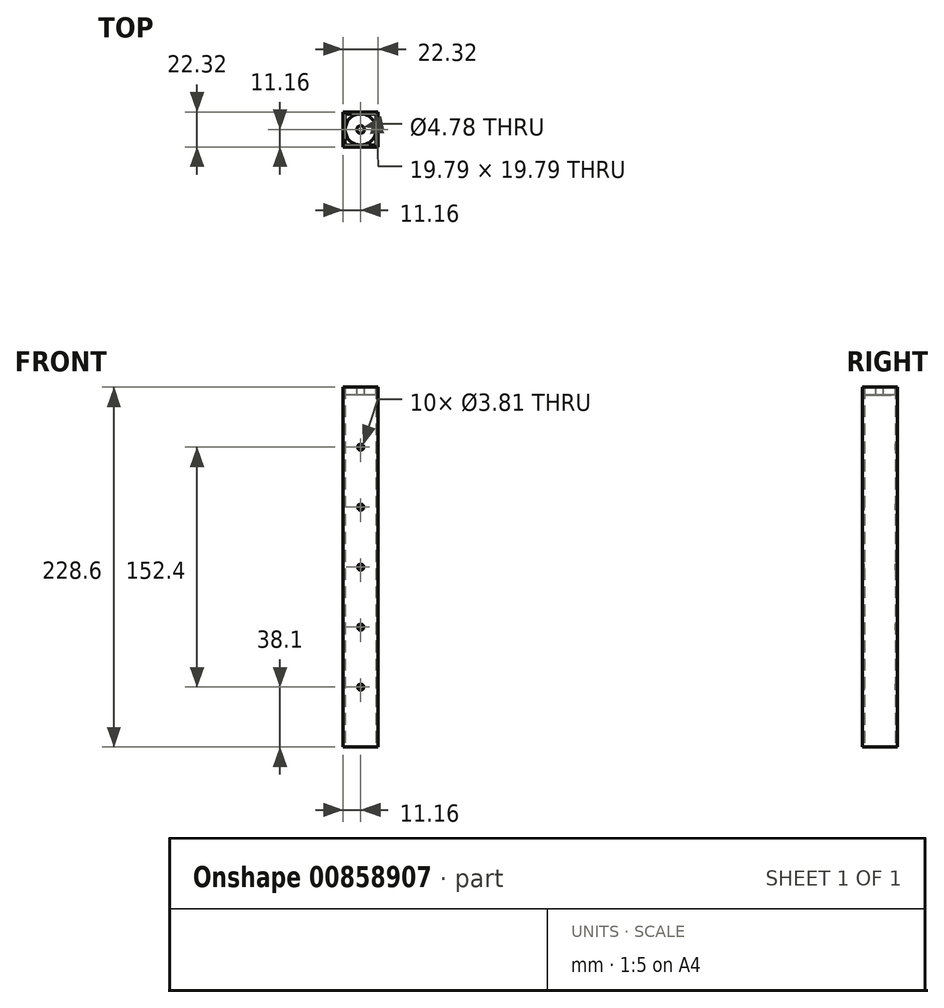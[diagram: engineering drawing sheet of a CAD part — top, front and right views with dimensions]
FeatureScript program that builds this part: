
annotation { "Feature Type Name" : "Feature", "Feature Type Description" : "" }
export const myFeature = defineFeature(function(context is Context, id is Id, definition is map)
    precondition{}
    {
        {
            var Q0;
            Q0=qCreatedBy(makeId("Top.planeOp"),FACE);
            var sketch = newSketch(context, id + "F0", { "sketchPlane" : qUnion([Q0])});
            skLineSegment(sketch, "E0.bottom", {"start": v(11.16, 11.16) * mm, "end": v(-11.16, 11.16) * mm});
            skLineSegment(sketch, "E0.top", {"start": v(11.16, -11.16) * mm, "end": v(-11.16, -11.16) * mm});
            skLineSegment(sketch, "E0.left", {"start": v(11.16, 11.16) * mm, "end": v(11.16, -11.16) * mm});
            skLineSegment(sketch, "E0.right", {"start": v(-11.16, 11.16) * mm, "end": v(-11.16, -11.16) * mm});
            skPoint(sketch, "E0.middle", {"position": v(0, 0) * mm});
            skLineSegment(sketch, "E1.bottom", {"start": v(9.9, 9.9) * mm, "end": v(-9.9, 9.9) * mm});
            skLineSegment(sketch, "E1.top", {"start": v(9.9, -9.9) * mm, "end": v(-9.9, -9.9) * mm});
            skLineSegment(sketch, "E1.left", {"start": v(9.9, 9.9) * mm, "end": v(9.9, -9.9) * mm});
            skLineSegment(sketch, "E1.right", {"start": v(-9.9, 9.9) * mm, "end": v(-9.9, -9.9) * mm});
            skSolve(sketch);
        }
        {
            var Q0;
            Q0 = qSketchRegion(id + "F0", true);
            extrude(context, id + "F1", {"entities" : qUnion([Q0]), "depth" : 228.6 * mm, "offsetDistance" : 25.4 * mm});
        }
        {
            var Q0;
            Q0=makeQuery(id+"F1.opExtrude","SWEPT_FACE",FACE,{"disambiguationData":[OSD([sQuery(id+"F0.wireOp",EDGE,"E0.top")])]});
            var sketch = newSketch(context, id + "F2", { "sketchPlane" : qUnion([Q0])});
            skCircle(sketch, "E2", {"center": v(0, 38.1) * mm, "radius": 1.9 * mm});
            skCircle(sketch, "E3.0.1.0", {"center": v(0, 76.2) * mm, "radius": 1.9 * mm});
            skCircle(sketch, "E3.0.2.0", {"center": v(0, 114.3) * mm, "radius": 1.9 * mm});
            skCircle(sketch, "E3.0.3.0", {"center": v(0, 152.4) * mm, "radius": 1.9 * mm});
            skCircle(sketch, "E3.0.4.0", {"center": v(0, 190.5) * mm, "radius": 1.9 * mm});
            skLineSegment(sketch, "E3.direction1", {"start": v(0, 38.1) * mm, "end": v(25.4, 38.1) * mm, "construction": true});
            skLineSegment(sketch, "E3.direction2", {"start": v(0, 38.1) * mm, "end": v(0, 76.2) * mm, "construction": true});
            skSolve(sketch);
        }
        {
            var Q0;
            Q0 = qSketchRegion(id + "F2", true);
            extrude(context, id + "F3", {"entities" : qUnion([Q0]), "operationType" : NewBodyOperationType.REMOVE, "endBound" : BoundingType.THROUGH_ALL, "oppositeDirection" : true, "depth" : 25.4 * mm, "offsetDistance" : 25.4 * mm});
        }
        {
            var Q0;
            Q0=makeQuery(id+"F1.opExtrude","CAP_FACE",FACE,{"disambiguationData":[OSD([sQuery(id+"F0.wireOp",EDGE,"E0.bottom"),sQuery(id+"F0.wireOp",EDGE,"E0.top"),sQuery(id+"F0.wireOp",EDGE,"E0.left"),sQuery(id+"F0.wireOp",EDGE,"E0.right"),sQuery(id+"F0.wireOp",EDGE,"E1.bottom"),sQuery(id+"F0.wireOp",EDGE,"E1.top"),sQuery(id+"F0.wireOp",EDGE,"E1.left"),sQuery(id+"F0.wireOp",EDGE,"E1.right")])],"isStart":false});
            var sketch = newSketch(context, id + "F4", { "sketchPlane" : qUnion([Q0])});
            skCircle(sketch, "E4", {"center": v(0, 0) * mm, "radius": 9.9 * mm});
            skCircle(sketch, "E5", {"center": v(0, 0) * mm, "radius": 2.39 * mm});
            skSolve(sketch);
        }
        {
            var Q0;
            Q0 = qSketchRegion(id + "F4", true);
            extrude(context, id + "F5", {"entities" : qUnion([Q0]), "operationType" : NewBodyOperationType.ADD, "oppositeDirection" : true, "depth" : 5.08 * mm, "offsetDistance" : 25.4 * mm});
        }
    });
